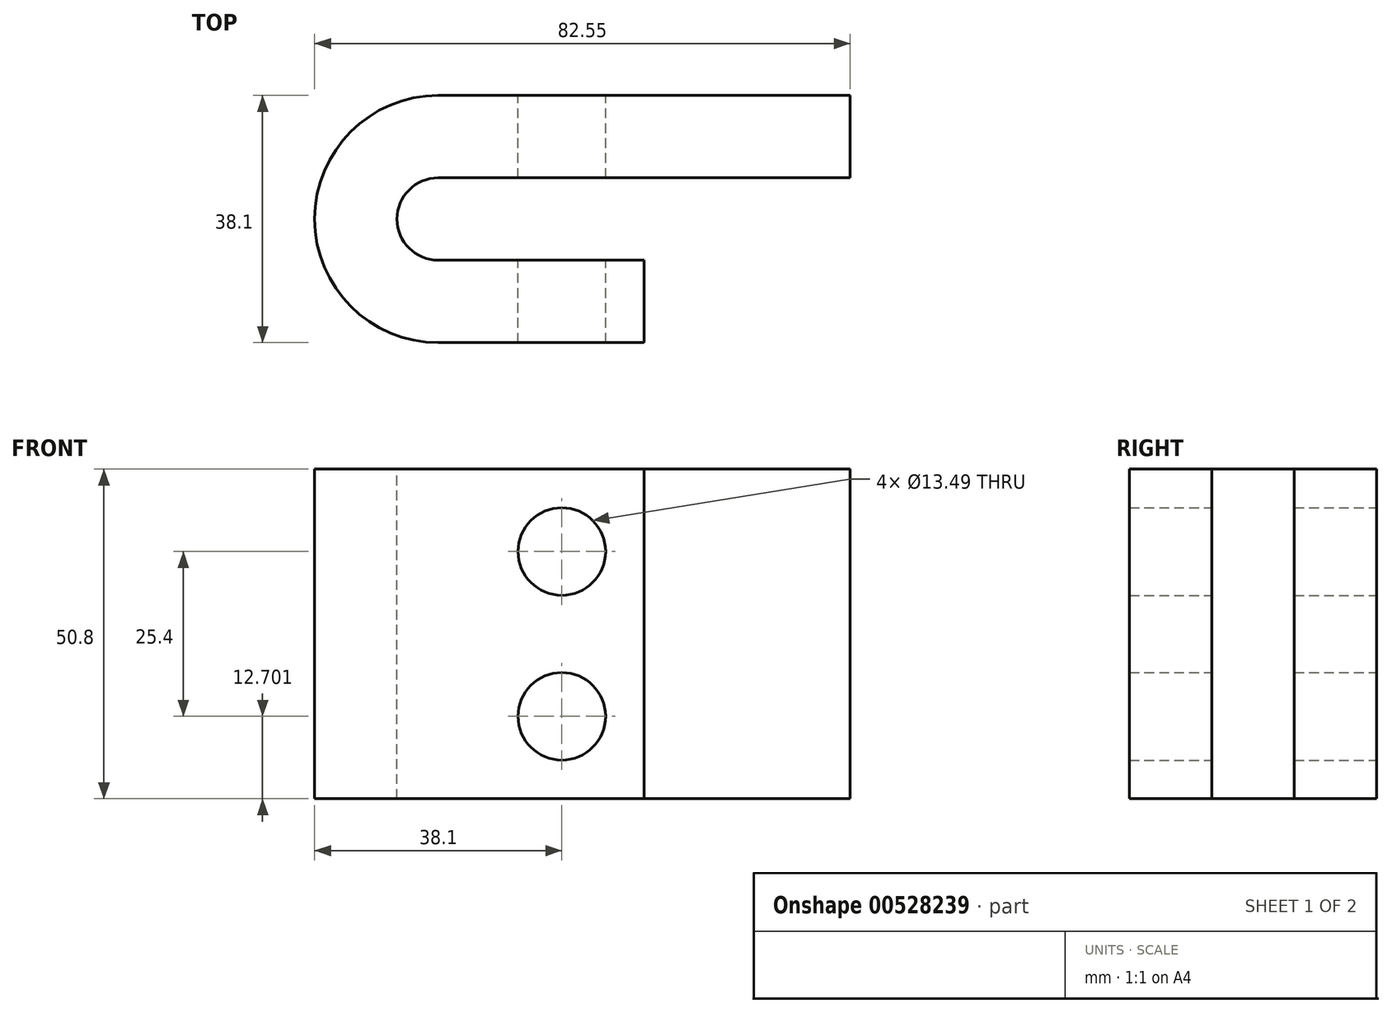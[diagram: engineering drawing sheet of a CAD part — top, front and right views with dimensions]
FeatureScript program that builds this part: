
annotation { "Feature Type Name" : "Feature", "Feature Type Description" : "" }
export const myFeature = defineFeature(function(context is Context, id is Id, definition is map)
    precondition{}
    {
        {
            var Q0;
            Q0=qCreatedBy(makeId("Front.planeOp"),FACE);
            var sketch = newSketch(context, id + "F0", { "sketchPlane" : qUnion([Q0])});
            skLineSegment(sketch, "E0.bottom", {"start": v(-19.05, 40.97) * mm, "end": v(-6.35, 40.97) * mm});
            skLineSegment(sketch, "E0.top", {"start": v(-19.05, -9.83) * mm, "end": v(-6.35, -9.83) * mm});
            skLineSegment(sketch, "E0.left", {"start": v(-19.05, 40.97) * mm, "end": v(-19.05, -9.83) * mm});
            skLineSegment(sketch, "E0.right", {"start": v(-6.35, 40.97) * mm, "end": v(-6.35, -9.83) * mm});
            skLineSegment(sketch, "E1", {"start": v(0, 40.97) * mm, "end": v(0, -9.83) * mm});
            skSolve(sketch);
        }
        {
            var Q0;
            Q0=makeQuery(id+"F0.imprint","IMPRINT",FACE,{"disambiguationData":[TD([[makeQuery(id+"F0.imprint","IMPRINT",EDGE,{"derivedFrom":sQuery(id+"F0.wireOp",EDGE,"E0.bottom")}),-1.0]])]});
            var Q1;
            Q1=sQuery(id+"F0.wireOp",EDGE,"E1");
            revolve(context, id + "F1", {"entities" : qUnion([Q0]), "axis" : qUnion([Q1]), "revolveType" : RevolveType.SYMMETRIC, "angle" : 180 * degree});
        }
        {
            var Q0;
            Q0=makeQuery(id+"F1.opRevolve","CAP_FACE",FACE,{"disambiguationData":[OSD([sQuery(id+"F0.wireOp",EDGE,"E0.bottom"),sQuery(id+"F0.wireOp",EDGE,"E0.top"),sQuery(id+"F0.wireOp",EDGE,"E0.left"),sQuery(id+"F0.wireOp",EDGE,"E0.right")])],"isStart":false});
            extrude(context, id + "F2", {"entities" : qUnion([Q0]), "operationType" : NewBodyOperationType.ADD, "depth" : 63.5 * mm, "offsetDistance" : 25.4 * mm});
        }
        {
            var Q0;
            Q0=makeQuery(id+"F1.opRevolve","CAP_FACE",FACE,{"disambiguationData":[OSD([sQuery(id+"F0.wireOp",EDGE,"E0.bottom"),sQuery(id+"F0.wireOp",EDGE,"E0.top"),sQuery(id+"F0.wireOp",EDGE,"E0.left"),sQuery(id+"F0.wireOp",EDGE,"E0.right")])],"isStart":true});
            extrude(context, id + "F3", {"entities" : qUnion([Q0]), "operationType" : NewBodyOperationType.ADD, "depth" : 31.75 * mm, "offsetDistance" : 25.4 * mm});
        }
        {
            var Q0;
            Q0=makeQuery(id+"F2.opExtrude","SWEPT_FACE",FACE,{"disambiguationData":[OSD([sQuery(id+"F0.wireOp",EDGE,"E0.left")])]});
            var sketch = newSketch(context, id + "F4", { "sketchPlane" : qUnion([Q0])});
            skPoint(sketch, "E2", {"position": v(-19.05, 2.87) * mm});
            skPoint(sketch, "E3", {"position": v(-19.05, 28.27) * mm});
            skSolve(sketch);
        }
        {
            var Q0;
            Q0=sQuery(id+"F4.wireOp",VERTEX,"E2");
            var Q1;
            Q1=sQuery(id+"F4.wireOp",VERTEX,"E3");
            var Q2;
            Q2=makeQuery(id+"F1.opRevolve","SWEPT_BODY",BODY,{"disambiguationData":[OSD([sQuery(id+"F0.wireOp",EDGE,"E0.bottom"),sQuery(id+"F0.wireOp",EDGE,"E0.top"),sQuery(id+"F0.wireOp",EDGE,"E0.left"),sQuery(id+"F0.wireOp",EDGE,"E0.right")])]});
            hole(context, id + "F5", {"style" : HoleStyle.SIMPLE, "endStyle" : HoleEndStyle.THROUGH, "standardTappedOrClearance" : lookupTablePath({ "standard" : "ANSI", "fit" : "Normal (ASME)", "size" : "1/2", "type" : "Clearance" }), "standardBlindInLast" : lookupTablePath({ "fit" : "Free", "standard" : "ANSI", "size" : "1/2", "type" : "Clearance" }), "holeDiameter" : 13.5 * mm, "isTappedThrough" : true, "tappedDepth" : 12.7 * mm, "tapClearance" : 3, "locations" : qUnion([Q0, Q1]), "scope" : qUnion([Q2])});
        }
    });
